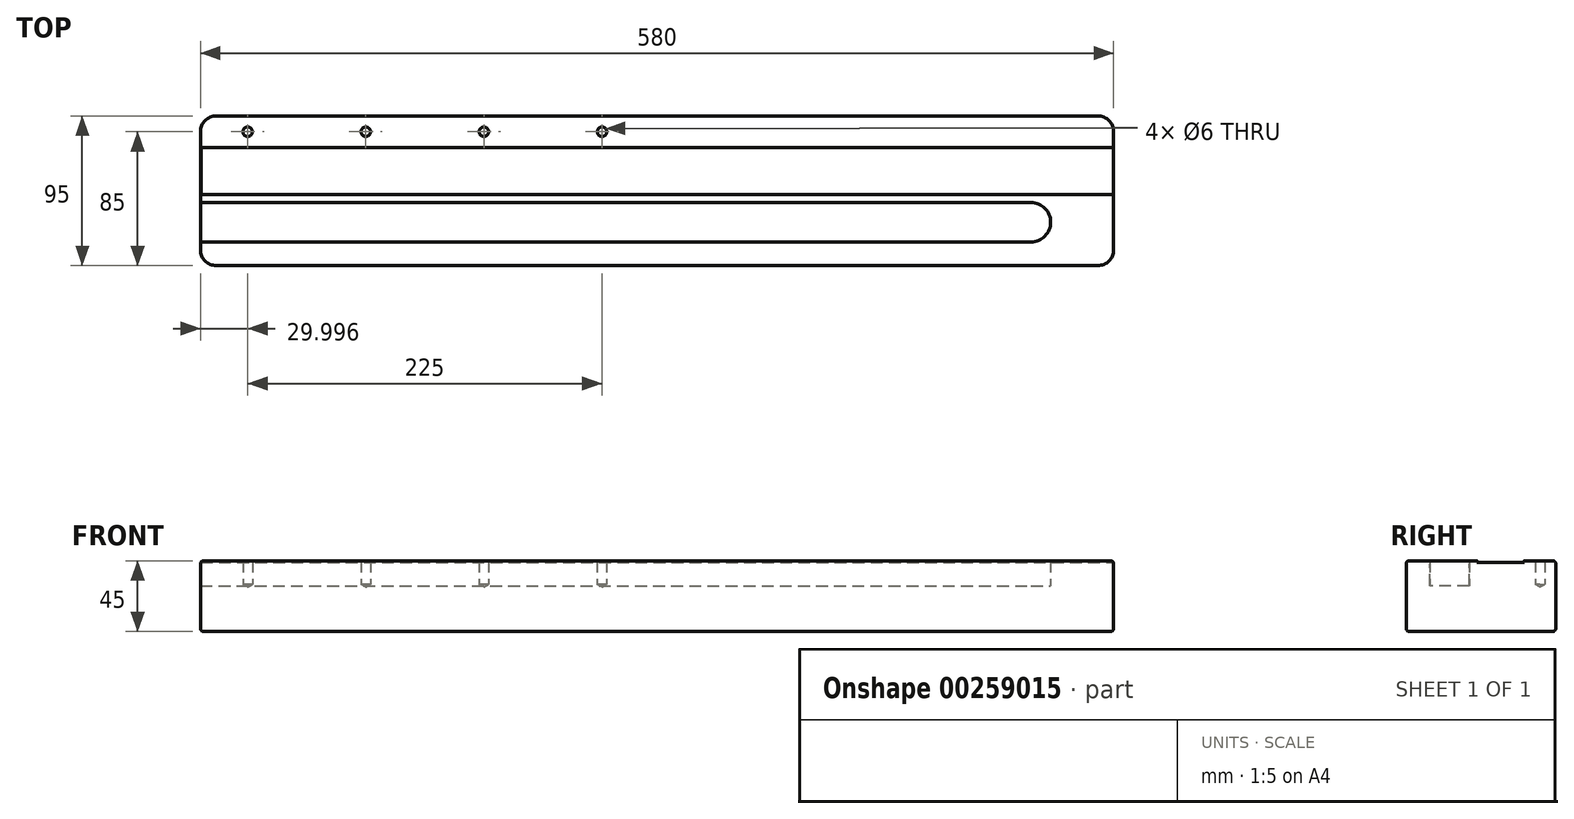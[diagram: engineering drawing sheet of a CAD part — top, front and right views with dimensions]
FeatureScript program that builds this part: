
annotation { "Feature Type Name" : "Feature", "Feature Type Description" : "" }
export const myFeature = defineFeature(function(context is Context, id is Id, definition is map)
    precondition{}
    {
        {
            var Q0;
            Q0=qCreatedBy(makeId("Top.planeOp"),FACE);
            var sketch = newSketch(context, id + "F0", { "sketchPlane" : qUnion([Q0])});
            skLineSegment(sketch, "E0.bottom", {"start": v(-246.05, -493.64) * mm, "end": v(333.95, -493.64) * mm});
            skLineSegment(sketch, "E0.top", {"start": v(-246.05, -398.64) * mm, "end": v(333.95, -398.64) * mm});
            skLineSegment(sketch, "E0.left", {"start": v(-246.05, -493.64) * mm, "end": v(-246.05, -398.64) * mm});
            skLineSegment(sketch, "E0.right", {"start": v(333.95, -493.64) * mm, "end": v(333.95, -398.64) * mm});
            skSolve(sketch);
        }
        {
            var Q0;
            Q0=makeQuery(id+"F0.imprint","IMPRINT",FACE,{"disambiguationData":[TD([[makeQuery(id+"F0.imprint","IMPRINT",EDGE,{"derivedFrom":sQuery(id+"F0.wireOp",EDGE,"E0.bottom")}),1.0]])]});
            extrude(context, id + "F1", {"entities" : qUnion([Q0]), "depth" : 45 * mm, "offsetDistance" : 25 * mm});
        }
        {
            var Q0;
            Q0=makeQuery(id+"F1.opExtrude","SWEPT_FACE",FACE,{"disambiguationData":[OSD([sQuery(id+"F0.wireOp",EDGE,"E0.right")])]});
            var sketch = newSketch(context, id + "F2", { "sketchPlane" : qUnion([Q0])});
            skLineSegment(sketch, "E1.bottom", {"start": v(-478.64, 45) * mm, "end": v(-453.64, 45) * mm});
            skLineSegment(sketch, "E1.top", {"start": v(-478.64, 29) * mm, "end": v(-453.64, 29) * mm});
            skLineSegment(sketch, "E1.left", {"start": v(-478.64, 45) * mm, "end": v(-478.64, 29) * mm});
            skLineSegment(sketch, "E1.right", {"start": v(-453.64, 45) * mm, "end": v(-453.64, 29) * mm});
            skSolve(sketch);
        }
        {
            var Q0;
            Q0=makeQuery(id+"F2.imprint","IMPRINT",FACE,{"disambiguationData":[TD([[makeQuery(id+"F2.imprint","IMPRINT",EDGE,{"derivedFrom":sQuery(id+"F2.wireOp",EDGE,"E1.bottom")}),-1.0]])]});
            extrude(context, id + "F3", {"entities" : qUnion([Q0]), "operationType" : NewBodyOperationType.REMOVE, "endBound" : BoundingType.THROUGH_ALL, "oppositeDirection" : true, "depth" : 560 * mm, "offsetDistance" : 25 * mm, "hasSecondDirection" : true, "secondDirectionOppositeDirection" : true, "secondDirectionDepth" : 40 * mm});
        }
        {
            var Q0;
            {var subQ0=sQuery(id+"F0.wireOp",EDGE,"E0.top");var subQ1=sQuery(id+"F0.wireOp",EDGE,"E0.left");var subQ2=sQuery(id+"F0.wireOp",EDGE,"E0.right");Q0=makeQuery(id+"F3.boolean.opBoolean","SPLIT",FACE,{"disambiguationData":[TD([makeQuery(id+"F1.opExtrude","SWEPT_FACE",FACE,{"disambiguationData":[OSD([subQ0])]})])],"derivedFrom":makeQuery(id+"F1.opExtrude","CAP_FACE",FACE,{"disambiguationData":[OSD([sQuery(id+"F0.wireOp",EDGE,"E0.bottom"),subQ0,subQ1,subQ2])],"isStart":false})});}
            var sketch = newSketch(context, id + "F4", { "sketchPlane" : qUnion([Q0])});
            skPoint(sketch, "E2", {"position": v(-216.05, -408.64) * mm});
            skPoint(sketch, "E3", {"position": v(-141.05, -408.64) * mm});
            skPoint(sketch, "E4", {"position": v(-66.05, -408.64) * mm});
            skPoint(sketch, "E5", {"position": v(8.95, -408.64) * mm});
            skLineSegment(sketch, "E6", {"start": v(-246.05, -408.64) * mm, "end": v(333.95, -408.64) * mm, "construction": true});
            skSolve(sketch);
        }
        {
            var Q0;
            Q0=makeQuery(id+"F1.opExtrude","SWEPT_FACE",FACE,{"disambiguationData":[OSD([sQuery(id+"F0.wireOp",EDGE,"E0.right")])]});
            var sketch = newSketch(context, id + "F5", { "sketchPlane" : qUnion([Q0])});
            skLineSegment(sketch, "E7.bottom", {"start": v(-448.64, 44) * mm, "end": v(-418.64, 44) * mm});
            skLineSegment(sketch, "E7.top", {"start": v(-448.64, 45) * mm, "end": v(-418.64, 45) * mm});
            skLineSegment(sketch, "E7.left", {"start": v(-448.64, 44) * mm, "end": v(-448.64, 45) * mm});
            skLineSegment(sketch, "E7.right", {"start": v(-418.64, 44) * mm, "end": v(-418.64, 45) * mm});
            skPoint(sketch, "E7.middle", {"position": v(-433.64, 44.5) * mm});
            skLineSegment(sketch, "E8.0.1", {"start": v(-453.64, 29) * mm, "end": v(-453.64, 45) * mm});
            skLineSegment(sketch, "E8.0.3", {"start": v(-453.64, 45) * mm, "end": v(-453.64, 29) * mm});
            skSolve(sketch);
        }
        {
            var Q0;
            Q0=sQuery(id+"F4.wireOp",VERTEX,"E2");
            var Q1;
            Q1=sQuery(id+"F4.wireOp",VERTEX,"E3");
            var Q2;
            Q2=sQuery(id+"F4.wireOp",VERTEX,"E4");
            var Q3;
            Q3=sQuery(id+"F4.wireOp",VERTEX,"E5");
            var Q4;
            Q4=makeQuery(id+"F1.opExtrude","SWEPT_BODY",BODY,{"disambiguationData":[OSD([sQuery(id+"F0.wireOp",EDGE,"E0.bottom"),sQuery(id+"F0.wireOp",EDGE,"E0.top"),sQuery(id+"F0.wireOp",EDGE,"E0.left"),sQuery(id+"F0.wireOp",EDGE,"E0.right")])]});
            hole(context, id + "F6", {"style" : HoleStyle.SIMPLE, "endStyle" : HoleEndStyle.BLIND, "holeDiameter" : 6 * mm, "majorDiameter" : 5 * mm, "holeDepth" : 15 * mm, "isTappedThrough" : true, "tappedDepth" : 12 * mm, "tapClearance" : 3, "startFromSketch" : true, "locations" : qUnion([Q0, Q1, Q2, Q3]), "scope" : qUnion([Q4])});
        }
        {
            var Q0;
            Q0=makeQuery(id+"F1.opExtrude","SWEPT_EDGE",EDGE,{"disambiguationData":[OSD([sQuery(id+"F0.wireOp",EDGE,"E0.bottom"),sQuery(id+"F0.wireOp",EDGE,"E0.left")])]});
            var Q1;
            Q1=makeQuery(id+"F1.opExtrude","SWEPT_EDGE",EDGE,{"disambiguationData":[OSD([sQuery(id+"F0.wireOp",EDGE,"E0.bottom"),sQuery(id+"F0.wireOp",EDGE,"E0.right")])]});
            var Q2;
            Q2=makeQuery(id+"F1.opExtrude","SWEPT_EDGE",EDGE,{"disambiguationData":[OSD([sQuery(id+"F0.wireOp",EDGE,"E0.top"),sQuery(id+"F0.wireOp",EDGE,"E0.right")])]});
            var Q3;
            Q3=makeQuery(id+"F1.opExtrude","SWEPT_EDGE",EDGE,{"disambiguationData":[OSD([sQuery(id+"F0.wireOp",EDGE,"E0.top"),sQuery(id+"F0.wireOp",EDGE,"E0.left")])]});
            fillet(context, id + "F7", {"entities" : qUnion([Q0, Q1, Q2, Q3]), "radius" : 10 * mm, "tangentPropagation" : true, "allowEdgeOverflow" : false});
        }
        {
            var Q0;
            Q0=makeQuery(id+"F1.opExtrude","CAP_EDGE",EDGE,{"disambiguationData":[OSD([sQuery(id+"F0.wireOp",EDGE,"E0.top")])],"isStart":false});
            var Q1;
            Q1=makeQuery(id+"F1.opExtrude","CAP_EDGE",EDGE,{"disambiguationData":[OSD([sQuery(id+"F0.wireOp",EDGE,"E0.bottom")])],"isStart":false});
            var Q2;
            Q2=makeQuery(id+"F1.opExtrude","CAP_EDGE",EDGE,{"disambiguationData":[OSD([sQuery(id+"F0.wireOp",EDGE,"E0.bottom")])],"isStart":true});
            fillet(context, id + "F8", {"entities" : qUnion([Q0, Q1, Q2]), "radius" : 2 * mm, "tangentPropagation" : true, "allowEdgeOverflow" : false});
        }
        {
            var Q0;
            Q0=makeQuery(id+"F3.boolean.opBoolean","COPY",EDGE,{"derivedFrom":makeQuery(id+"F3.opExtrude","CAP_EDGE",EDGE,{"disambiguationData":[OSD([sQuery(id+"F2.wireOp",EDGE,"E1.right")])],"isStart":true})});
            var Q1;
            Q1=makeQuery(id+"F3.boolean.opBoolean","COPY",EDGE,{"derivedFrom":makeQuery(id+"F3.opExtrude","CAP_EDGE",EDGE,{"disambiguationData":[OSD([sQuery(id+"F2.wireOp",EDGE,"E1.left")])],"isStart":true})});
            fillet(context, id + "F9", {"entities" : qUnion([Q0, Q1]), "radius" : 12.5 * mm, "tangentPropagation" : true, "allowEdgeOverflow" : false});
        }
        {
            var Q0;
            Q0=makeQuery(id+"F5.imprint","IMPRINT",FACE,{"disambiguationData":[TD([[makeQuery(id+"F5.imprint","IMPRINT",EDGE,{"derivedFrom":sQuery(id+"F5.wireOp",EDGE,"E7.bottom")}),1.0]])]});
            extrude(context, id + "F10", {"entities" : qUnion([Q0]), "operationType" : NewBodyOperationType.REMOVE, "endBound" : BoundingType.THROUGH_ALL, "oppositeDirection" : true, "depth" : 25 * mm, "offsetDistance" : 25 * mm});
        }
    });
